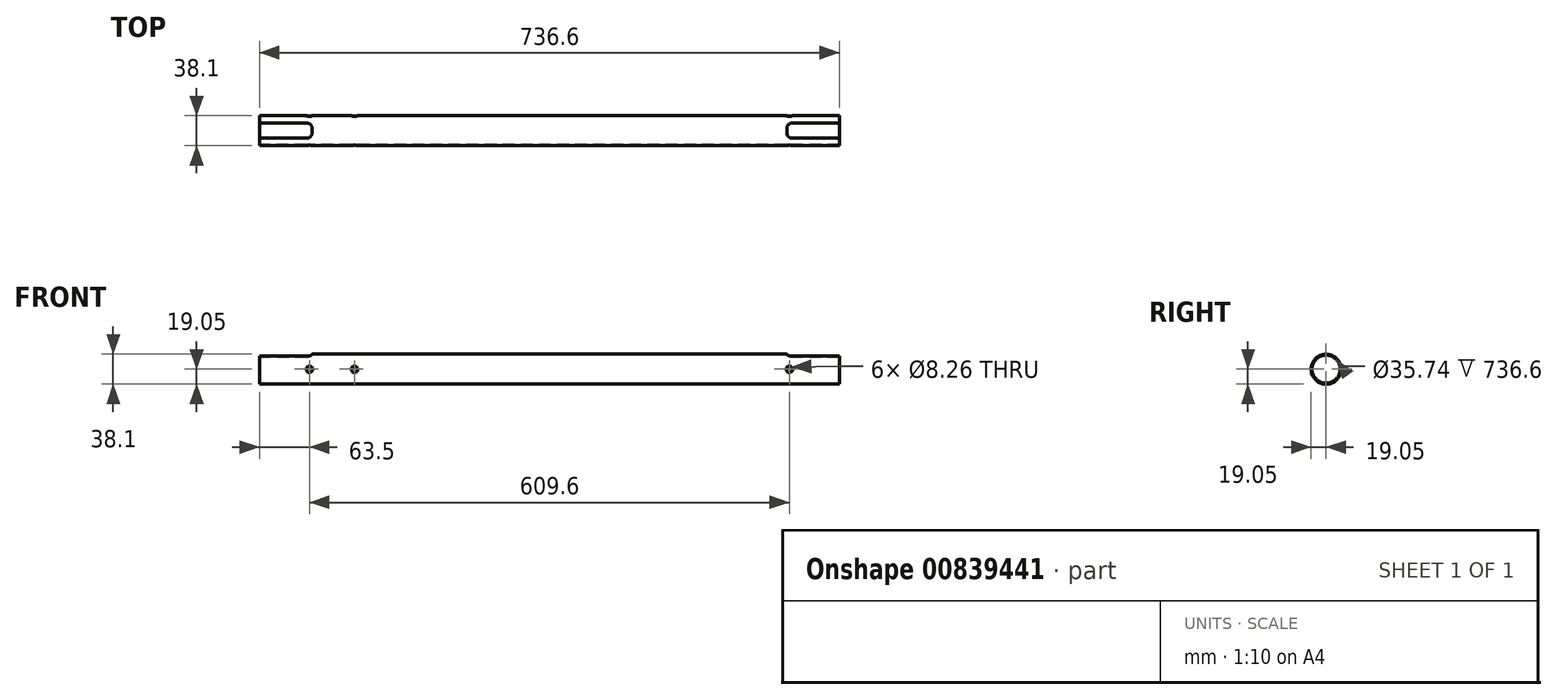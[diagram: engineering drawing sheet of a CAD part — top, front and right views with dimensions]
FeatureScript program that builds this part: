
annotation { "Feature Type Name" : "Feature", "Feature Type Description" : "" }
export const myFeature = defineFeature(function(context is Context, id is Id, definition is map)
    precondition{}
    {
        {
            var Q0;
            Q0=qCreatedBy(makeId("Right.planeOp"),FACE);
            var sketch = newSketch(context, id + "F0", { "sketchPlane" : qUnion([Q0])});
            skCircle(sketch, "E0", {"center": v(0, 0) * mm, "radius": 19.05 * mm});
            skCircle(sketch, "E1", {"center": v(0, 0) * mm, "radius": 17.87 * mm});
            skSolve(sketch);
        }
        {
            var Q0;
            Q0=makeQuery(id+"F0.imprint","IMPRINT",FACE,{"disambiguationData":[TD([[makeQuery(id+"F0.imprint","IMPRINT",EDGE,{"derivedFrom":sQuery(id+"F0.wireOp",EDGE,"E0")}),1.0]])]});
            extrude(context, id + "F1", {"entities" : qUnion([Q0]), "depth" : 736.6 * mm, "offsetDistance" : 25.4 * mm, "symmetric" : true});
        }
        {
            var Q0;
            Q0=qCreatedBy(makeId("Front.planeOp"),FACE);
            var sketch = newSketch(context, id + "F2", { "sketchPlane" : qUnion([Q0])});
            skCircle(sketch, "E2", {"center": v(-304.8, 0) * mm, "radius": 4.13 * mm});
            skCircle(sketch, "E3.MirrorC", {"center": v(304.8, 0) * mm, "radius": 4.13 * mm});
            skCircle(sketch, "E4", {"center": v(-247.65, 0) * mm, "radius": 4.13 * mm});
            skSolve(sketch);
        }
        {
            var Q0;
            Q0 = qSketchRegion(id + "F2", true);
            extrude(context, id + "F3", {"entities" : qUnion([Q0]), "operationType" : NewBodyOperationType.REMOVE, "endBound" : BoundingType.THROUGH_ALL, "oppositeDirection" : true, "depth" : 25.4 * mm, "offsetDistance" : 25.4 * mm, "hasSecondDirection" : true, "secondDirectionBound" : BoundingType.THROUGH_ALL, "secondDirectionOppositeDirection" : false, "secondDirectionDepth" : 25.4 * mm});
        }
        {
            var Q0;
            Q0=qCreatedBy(makeId("Top.planeOp"),FACE);
            var sketch = newSketch(context, id + "F4", { "sketchPlane" : qUnion([Q0])});
            skLineSegment(sketch, "E5.bottom", {"start": v(-301.63, -9.53) * mm, "end": v(-384.18, -9.53) * mm});
            skLineSegment(sketch, "E5.top", {"start": v(-301.63, 9.52) * mm, "end": v(-384.18, 9.52) * mm});
            skLineSegment(sketch, "E5.left", {"start": v(-301.63, -9.53) * mm, "end": v(-301.63, 9.52) * mm});
            skLineSegment(sketch, "E5.right", {"start": v(-384.18, -9.53) * mm, "end": v(-384.18, 9.52) * mm});
            skPoint(sketch, "E5.middle", {"position": v(-342.9, 0) * mm});
            skLineSegment(sketch, "E6.MirrorCS", {"start": v(301.63, -9.53) * mm, "end": v(301.63, 9.52) * mm});
            skLineSegment(sketch, "E7.MirrorCS", {"start": v(301.63, 9.52) * mm, "end": v(384.18, 9.52) * mm});
            skLineSegment(sketch, "E8.MirrorCS", {"start": v(301.63, -9.53) * mm, "end": v(384.18, -9.53) * mm});
            skLineSegment(sketch, "E9.MirrorCS", {"start": v(384.18, -9.53) * mm, "end": v(384.18, 9.52) * mm});
            skSolve(sketch);
        }
        {
            var Q0;
            Q0 = qSketchRegion(id + "F4", true);
            extrude(context, id + "F5", {"entities" : qUnion([Q0]), "operationType" : NewBodyOperationType.REMOVE, "endBound" : BoundingType.THROUGH_ALL, "depth" : 25.4 * mm, "offsetDistance" : 25.4 * mm});
        }
        {
            var Q0;
            Q0=makeQuery(id+"F5.boolean.opBoolean","COPY",EDGE,{"disambiguationData":[OD(1.0)],"derivedFrom":makeQuery(id+"F5.opExtrude","SWEPT_EDGE",EDGE,{"disambiguationData":[OSD([sQuery(id+"F4.wireOp",EDGE,"E5.top"),sQuery(id+"F4.wireOp",EDGE,"E5.left")])]})});
            var Q1;
            Q1=makeQuery(id+"F5.boolean.opBoolean","COPY",EDGE,{"disambiguationData":[OD(1.0)],"derivedFrom":makeQuery(id+"F5.opExtrude","SWEPT_EDGE",EDGE,{"disambiguationData":[OSD([sQuery(id+"F4.wireOp",EDGE,"E5.bottom"),sQuery(id+"F4.wireOp",EDGE,"E5.left")])]})});
            var Q2;
            Q2=makeQuery(id+"F5.boolean.opBoolean","COPY",EDGE,{"disambiguationData":[OD(0.0)],"derivedFrom":makeQuery(id+"F5.opExtrude","SWEPT_EDGE",EDGE,{"disambiguationData":[OSD([sQuery(id+"F4.wireOp",EDGE,"E5.top"),sQuery(id+"F4.wireOp",EDGE,"E5.left")])]})});
            var Q3;
            Q3=makeQuery(id+"F5.boolean.opBoolean","COPY",EDGE,{"disambiguationData":[OD(0.0)],"derivedFrom":makeQuery(id+"F5.opExtrude","SWEPT_EDGE",EDGE,{"disambiguationData":[OSD([sQuery(id+"F4.wireOp",EDGE,"E5.bottom"),sQuery(id+"F4.wireOp",EDGE,"E5.left")])]})});
            var Q4;
            Q4=makeQuery(id+"F5.boolean.opBoolean","COPY",EDGE,{"derivedFrom":makeQuery(id+"F5.opExtrude","SWEPT_EDGE",EDGE,{"disambiguationData":[OSD([sQuery(id+"F4.wireOp",EDGE,"E6.MirrorCS"),sQuery(id+"F4.wireOp",EDGE,"E7.MirrorCS")])]})});
            var Q5;
            Q5=makeQuery(id+"F5.boolean.opBoolean","COPY",EDGE,{"derivedFrom":makeQuery(id+"F5.opExtrude","SWEPT_EDGE",EDGE,{"disambiguationData":[OSD([sQuery(id+"F4.wireOp",EDGE,"E6.MirrorCS"),sQuery(id+"F4.wireOp",EDGE,"E8.MirrorCS")])]})});
            fillet(context, id + "F6", {"entities" : qUnion([Q0, Q1, Q2, Q3, Q4, Q5]), "tangentPropagation" : true, "radius" : 6.35 * mm, "defaultsChanged" : false, "vertexSettings" : [], "allowEdgeOverflow" : false});
        }
    });
